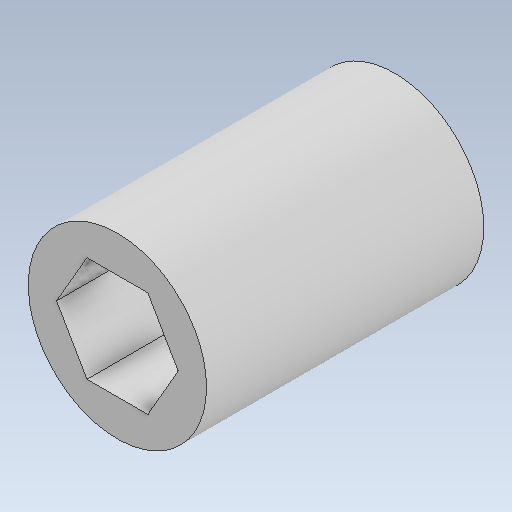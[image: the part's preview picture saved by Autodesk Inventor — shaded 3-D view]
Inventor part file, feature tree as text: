
AUTODESK INVENTOR PART (.ipt)
format: ipt  version: 2020.3 (Build 243373000, 373)  size: 124,928 bytes
history: native  units: mm
features: extrude x3, sketch x3, projected_geometry x1
ambient origin geometry x8: Origin, YZ Plane, XZ Plane, XY Plane, X Axis, Y Axis, Z Axis, Center Point
bodies: Solid1 (feature_tree)
feature tree (7):
  extrude  "Extrusion1"  Depth=25.0mm TaperAngle=0.0deg
  extrude  "Extrusion2"  Depth=13.3mm TaperAngle=0.0deg
  extrude  "Extrusion3"  [1 undecoded]
  sketch  "Sketch1"  dims[d0=22.5mm d1=25.0mm d2=0.0mm]
  sketch  "Sketch2"  dims[d3=13.3mm d4=30.0mm d5=0.0mm]
  sketch  "Sketch3"  dims[d6=10.0mm d7=0.0mm]
  projected_geometry  "Projected Loop1"
note: 1 required parameter value undecoded (feature->parameter linkage not recoverable at this tier; creation-order binding heuristic only, values carry confidence <= 0.55)
